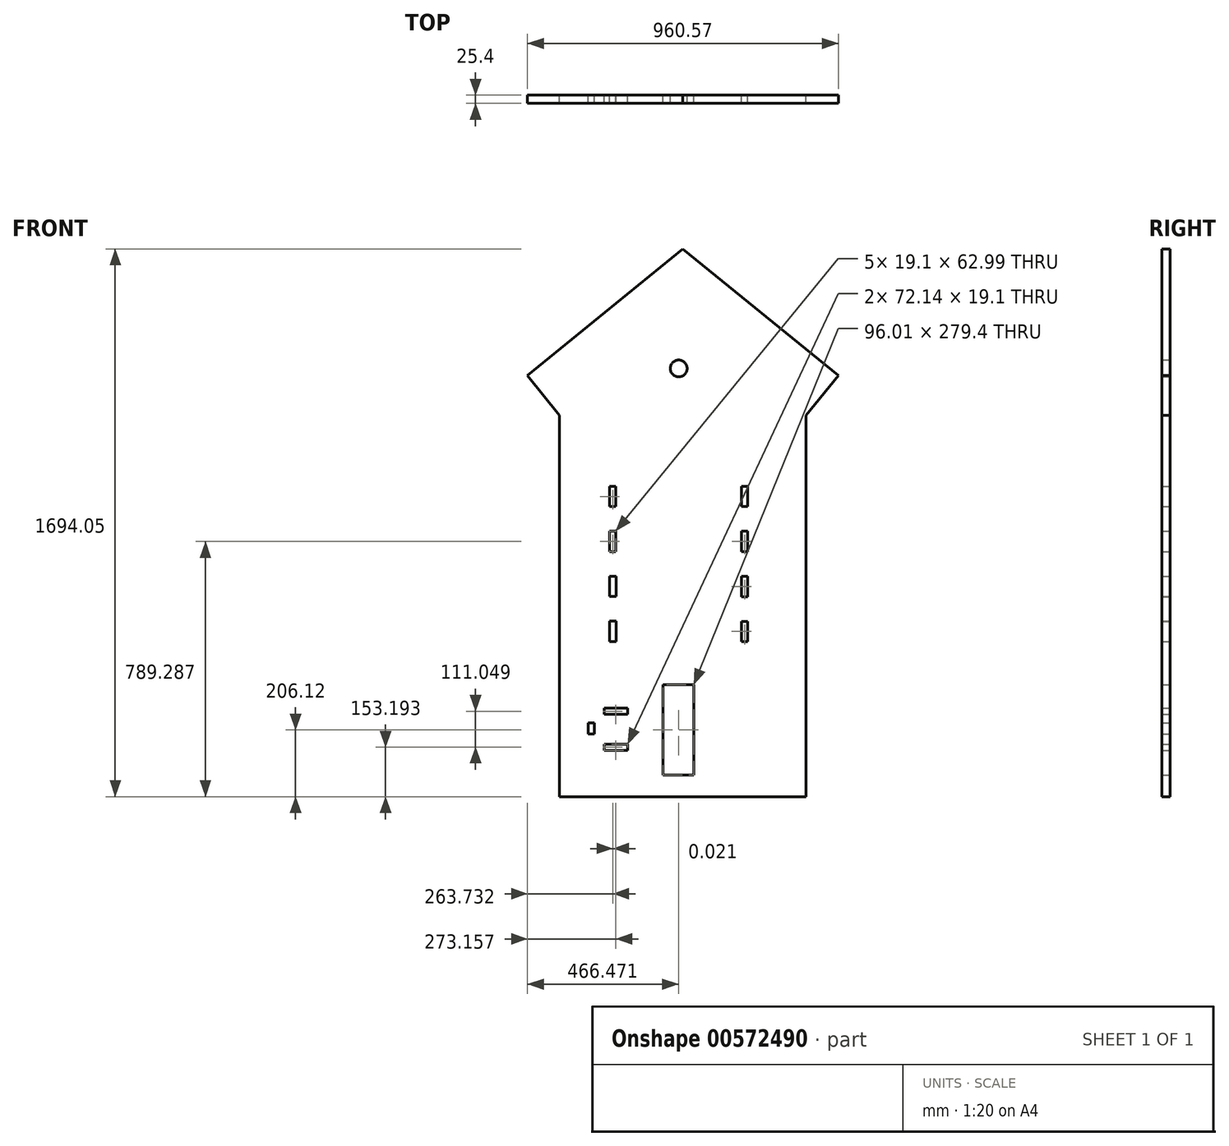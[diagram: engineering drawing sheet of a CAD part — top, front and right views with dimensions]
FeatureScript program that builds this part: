
annotation { "Feature Type Name" : "Feature", "Feature Type Description" : "" }
export const myFeature = defineFeature(function(context is Context, id is Id, definition is map)
    precondition{}
    {
        {
            var Q0;
            Q0=qCreatedBy(makeId("Front.planeOp"),FACE);
            var sketch = newSketch(context, id + "F0", { "sketchPlane" : qUnion([Q0])});
            skPoint(sketch, "E0.endSnap0", {"position": v(0, -100.27) * mm});
            skLineSegment(sketch, "E1.top", {"start": v(194.28, -315.77) * mm, "end": v(213.38, -315.77) * mm});
            skLineSegment(sketch, "E1.left", {"start": v(194.28, -378.76) * mm, "end": v(194.28, -315.77) * mm});
            skLineSegment(sketch, "E1.right", {"start": v(213.38, -378.76) * mm, "end": v(213.38, -315.77) * mm});
            skLineSegment(sketch, "E2.MirrorCS", {"start": v(-194.28, -315.77) * mm, "end": v(-213.38, -315.77) * mm});
            skLineSegment(sketch, "E3.MirrorCS", {"start": v(-213.38, -378.76) * mm, "end": v(-213.38, -315.77) * mm});
            skLineSegment(sketch, "E4.MirrorCS", {"start": v(-194.28, -378.76) * mm, "end": v(-194.28, -315.77) * mm});
            skLineSegment(sketch, "E5.MirrorCS", {"start": v(-194.28, -378.76) * mm, "end": v(-213.38, -378.76) * mm});
            skLineSegment(sketch, "E6.bottom", {"start": v(-230.47, -973.8) * mm, "end": v(-158.33, -973.8) * mm});
            skLineSegment(sketch, "E6.top", {"start": v(-230.47, -992.9) * mm, "end": v(-158.33, -992.9) * mm});
            skLineSegment(sketch, "E6.left", {"start": v(-230.47, -973.8) * mm, "end": v(-230.47, -992.9) * mm});
            skLineSegment(sketch, "E6.right", {"start": v(-158.33, -973.8) * mm, "end": v(-158.33, -992.9) * mm});
            skLineSegment(sketch, "E7.1.0.0", {"start": v(-194, -454.96) * mm, "end": v(-213.36, -454.96) * mm});
            skLineSegment(sketch, "E7.1.0.1", {"start": v(-194, -517.7) * mm, "end": v(-194, -454.96) * mm});
            skLineSegment(sketch, "E7.1.0.2", {"start": v(-194, -517.7) * mm, "end": v(-213.36, -517.7) * mm});
            skLineSegment(sketch, "E7.1.0.3", {"start": v(-213.36, -517.7) * mm, "end": v(-213.36, -454.96) * mm});
            skLineSegment(sketch, "E7.2.0.0", {"start": v(-193.9, -593.9) * mm, "end": v(-213.34, -593.9) * mm});
            skLineSegment(sketch, "E7.2.0.1", {"start": v(-193.9, -656.63) * mm, "end": v(-193.9, -593.9) * mm});
            skLineSegment(sketch, "E7.2.0.2", {"start": v(-193.9, -656.63) * mm, "end": v(-213.34, -656.63) * mm});
            skLineSegment(sketch, "E7.2.0.3", {"start": v(-213.34, -656.63) * mm, "end": v(-213.34, -593.9) * mm});
            skLineSegment(sketch, "E8.MirrorCS", {"start": v(193.93, -517.95) * mm, "end": v(213.03, -517.95) * mm});
            skLineSegment(sketch, "E9.MirrorCS", {"start": v(193.9, -594.15) * mm, "end": v(213, -594.15) * mm});
            skLineSegment(sketch, "E10.MirrorCS", {"start": v(193.9, -657.14) * mm, "end": v(213, -657.14) * mm});
            skLineSegment(sketch, "E11.MirrorCS", {"start": v(193.93, -454.96) * mm, "end": v(213.03, -454.96) * mm});
            skLineSegment(sketch, "E12.MirrorCS", {"start": v(213, -657.14) * mm, "end": v(213, -594.15) * mm});
            skLineSegment(sketch, "E13.MirrorCS", {"start": v(193.9, -657.14) * mm, "end": v(193.9, -594.15) * mm});
            skLineSegment(sketch, "E14.MirrorCS", {"start": v(193.93, -517.95) * mm, "end": v(193.93, -454.96) * mm});
            skLineSegment(sketch, "E15.MirrorCS", {"start": v(213.03, -517.95) * mm, "end": v(213.03, -454.96) * mm});
            skLineSegment(sketch, "E16.1.0.0", {"start": v(-194.26, -239.57) * mm, "end": v(-194.26, -176.57) * mm});
            skLineSegment(sketch, "E16.1.0.1", {"start": v(-213.36, -239.57) * mm, "end": v(-213.36, -176.57) * mm});
            skLineSegment(sketch, "E16.1.0.2", {"start": v(-194.26, -239.57) * mm, "end": v(-213.36, -239.57) * mm});
            skLineSegment(sketch, "E16.1.0.3", {"start": v(-194.26, -176.57) * mm, "end": v(-213.36, -176.57) * mm});
            skLineSegment(sketch, "E16.direction1", {"start": v(-213.38, -378.76) * mm, "end": v(-213.36, -239.57) * mm, "construction": true});
            skLineSegment(sketch, "E17.MirrorCS", {"start": v(213.36, -239.57) * mm, "end": v(213.36, -176.57) * mm});
            skLineSegment(sketch, "E18.MirrorCS", {"start": v(193.93, -239.57) * mm, "end": v(193.93, -176.57) * mm});
            skLineSegment(sketch, "E19.MirrorCS", {"start": v(193.93, -176.57) * mm, "end": v(213.36, -176.57) * mm});
            skLineSegment(sketch, "E20.MirrorCS", {"start": v(193.93, -239.57) * mm, "end": v(213.36, -239.57) * mm});
            skCircle(sketch, "E21", {"center": v(0, 187.76) * mm, "radius": 26.03 * mm});
            skLineSegment(sketch, "E22.bottom", {"start": v(46.92, -790.73) * mm, "end": v(-49.1, -790.73) * mm});
            skLineSegment(sketch, "E22.top", {"start": v(46.92, -1070.13) * mm, "end": v(-49.1, -1070.13) * mm});
            skLineSegment(sketch, "E22.left", {"start": v(46.92, -790.73) * mm, "end": v(46.92, -1070.13) * mm});
            skLineSegment(sketch, "E22.right", {"start": v(-49.1, -790.73) * mm, "end": v(-49.1, -1070.13) * mm});
            skLineSegment(sketch, "E23", {"start": v(-467.56, 166.42) * mm, "end": v(12.73, 557.5) * mm});
            skLineSegment(sketch, "E24", {"start": v(194.28, -378.76) * mm, "end": v(213.38, -378.76) * mm});
            skLineSegment(sketch, "E25", {"start": v(-158.33, -973.8) * mm, "end": v(-158.33, -788.76) * mm, "construction": true});
            skLineSegment(sketch, "E26.bottom", {"start": v(-158.33, -862.76) * mm, "end": v(-230.47, -862.76) * mm});
            skLineSegment(sketch, "E26.top", {"start": v(-158.33, -881.86) * mm, "end": v(-230.47, -881.86) * mm});
            skLineSegment(sketch, "E26.left", {"start": v(-158.33, -862.76) * mm, "end": v(-158.33, -881.86) * mm});
            skLineSegment(sketch, "E26.right", {"start": v(-230.47, -862.76) * mm, "end": v(-230.47, -881.86) * mm});
            skLineSegment(sketch, "E27.bottom", {"start": v(-260.67, -907.99) * mm, "end": v(-279.78, -907.99) * mm});
            skLineSegment(sketch, "E27.top", {"start": v(-260.67, -942.91) * mm, "end": v(-279.78, -942.91) * mm});
            skLineSegment(sketch, "E27.left", {"start": v(-260.67, -907.99) * mm, "end": v(-260.67, -942.91) * mm});
            skLineSegment(sketch, "E27.right", {"start": v(-279.78, -907.99) * mm, "end": v(-279.78, -942.91) * mm});
            skLineSegment(sketch, "E28", {"start": v(-368.27, -618.28) * mm, "end": v(-368.27, 42.78) * mm});
            skLineSegment(sketch, "E29", {"start": v(-368.27, -618.28) * mm, "end": v(-368.27, -1136.55) * mm});
            skLineSegment(sketch, "E30", {"start": v(12.73, 557.5) * mm, "end": v(12.73, -1192.31) * mm, "construction": true});
            skLineSegment(sketch, "E31.MirrorCS", {"start": v(493.01, 166.42) * mm, "end": v(12.73, 557.5) * mm});
            skLineSegment(sketch, "E32.MirrorCS", {"start": v(393.73, -618.28) * mm, "end": v(393.73, 42.78) * mm});
            skLineSegment(sketch, "E33.MirrorCS", {"start": v(393.73, -618.28) * mm, "end": v(393.73, -1136.55) * mm});
            skLineSegment(sketch, "E34", {"start": v(-368.27, -1136.55) * mm, "end": v(393.73, -1136.55) * mm});
            skLineSegment(sketch, "E35", {"start": v(-467.56, 166.42) * mm, "end": v(-368.27, 42.78) * mm});
            skLineSegment(sketch, "E36", {"start": v(493.01, 166.42) * mm, "end": v(393.73, 42.78) * mm});
            skSolve(sketch);
        }
        {
            var Q0;
            Q0=makeQuery(id+"F0.imprint","IMPRINT",FACE,{"disambiguationData":[TD([[makeQuery(id+"F0.imprint","IMPRINT",EDGE,{"derivedFrom":sQuery(id+"F0.wireOp",EDGE,"E1.top")}),1.0]])]});
            extrude(context, id + "F1", {"entities" : qUnion([Q0]), "depth" : 25.4 * mm, "offsetDistance" : 25.4 * mm});
        }
    });
